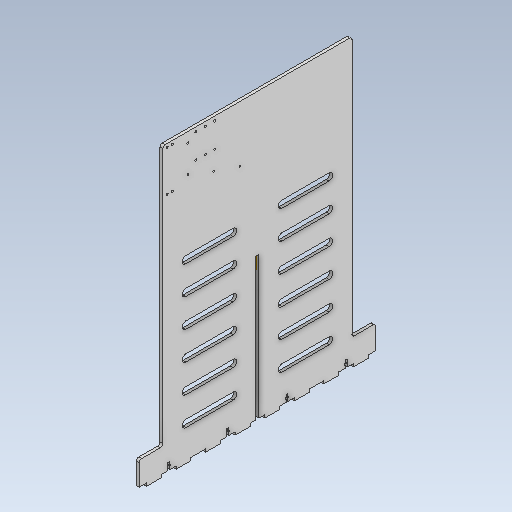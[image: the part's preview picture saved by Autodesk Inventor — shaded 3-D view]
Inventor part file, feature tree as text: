
AUTODESK INVENTOR PART (.ipt)
format: ipt  version: 2021.1 (Build 251245010, 245A)  size: 392,192 bytes
history: native  units: mm
features: reference x17, other x5, extrude x3, sketch x3
ambient origin geometry x8: Origin, YZ Plane, XZ Plane, XY Plane, X Axis, Y Axis, Z Axis, Center Point
bodies: Body1 (feature_tree)
feature tree (28):
  other  "Твердое тело1"
  other  "РабПлоскость1"
  extrude  "Корпус"  Depth=400.0mm
  extrude  "Отверстия"  Depth=500.0mm
  extrude  "Пазы"  Depth=6.0mm
  sketch  "Эскиз1"
  reference  "Ссылка1"
  reference  "Ссылка2"
  reference  "Ссылка3"
  reference  "Ссылка4"
  reference  "Ссылка5"
  reference  "Ссылка6"
  reference  "Ссылка7"
  reference  "Ссылка8"
  reference  "Ссылка9"
  reference  "Ссылка10"
  reference  "Ссылка11"
  reference  "Ссылка12"
  reference  "Ссылка13"
  reference  "Ссылка14"
  reference  "Ссылка15"
  reference  "Ссылка16"
  reference  "Ссылка17"
  sketch  "Эскиз2"
  sketch  "Эскиз3"
  other  "<userpath>\Documents\Savka\3d\Korp.iam"
  other  "Korp.iam"
  other  "Korpus:1"
